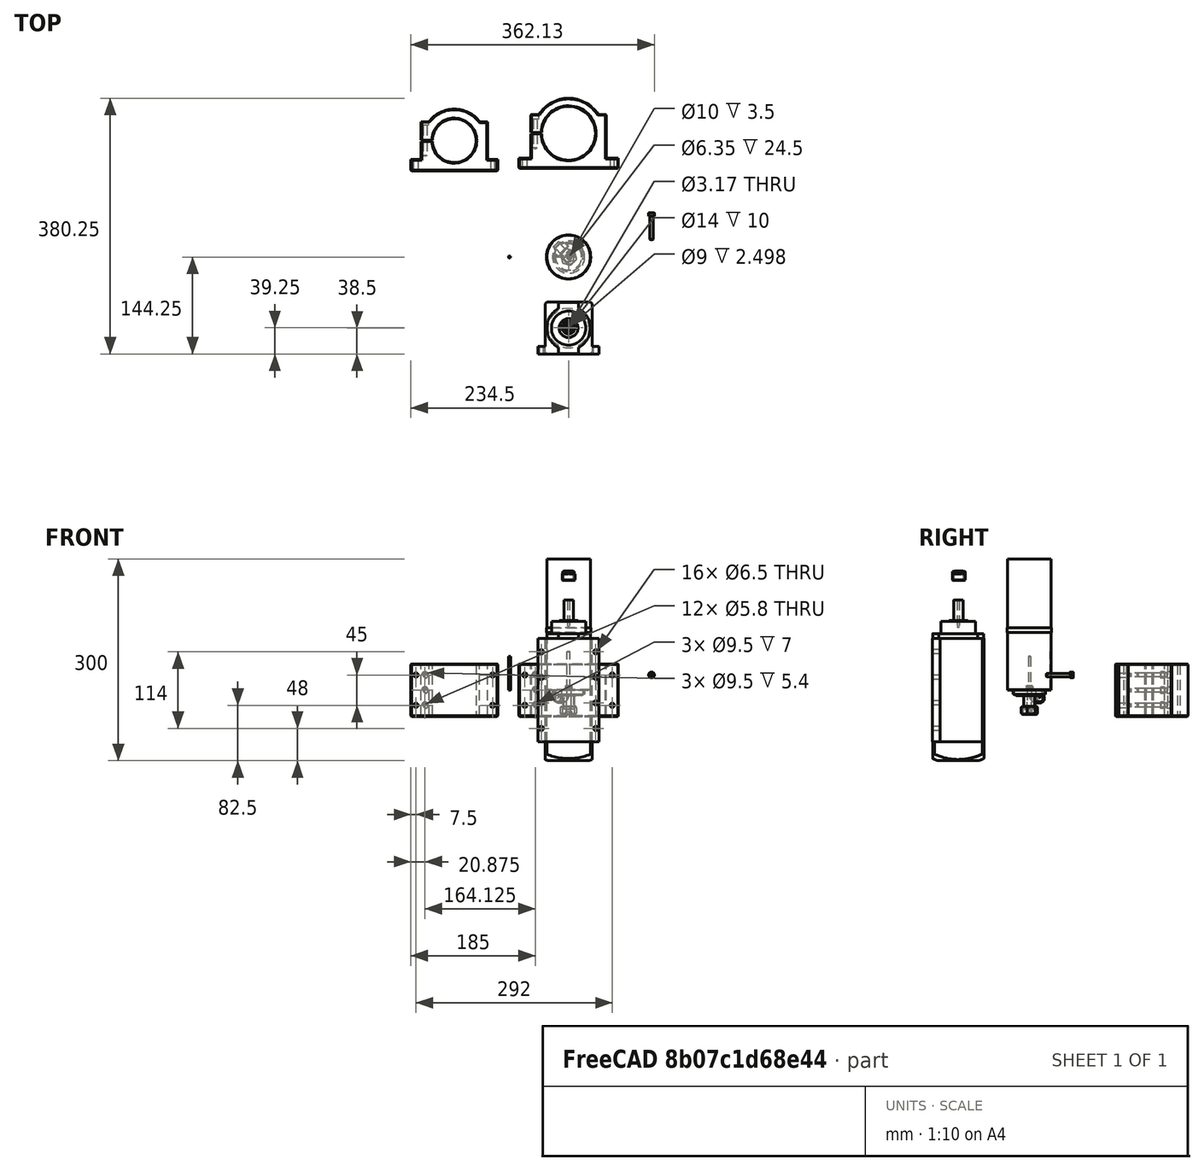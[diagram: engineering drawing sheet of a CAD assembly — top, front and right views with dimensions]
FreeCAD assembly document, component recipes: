
FREECAD ASSEMBLY — COMPONENT RECIPES ("Spindle")

This assembly document has 15 components, labeled P0..P14 below (a component is one placed body or linked part). 11 of them carry a construction recipe — the FreeCAD feature program that regenerates the part from scratch, quoted from this document or its linked companion documents; the rest are supplied as boundary geometry only. No exploded tour is included for this assembly.
COMPONENT P0 — recipe-attached ("80mm", modeled in this document).
Construction recipe (the document's own serialized feature program — sketch geometry with constraints, then the solid features built on it; lengths are millimeters unless a unit is written):

FEATURE [Sketcher::SketchObject] Sketch019
  FullyConstrained = true
  MapMode = 5
  Placement = pos=(0,0,0) rot=(1,0,0;1.5708rad)
  Support = -> [XZ_Plane005]
  sketch-geometry (18):
    g0: ArcOfCircle CenterX=0 CenterY=0 CenterZ=0 NormalX=0 NormalY=0 NormalZ=1 AngleXU=0 Radius=40 StartAngle=3.1666 EndAngle=9.39978
    g1: LineSegment StartX=-56 StartY=28 StartZ=0 EndX=-43.8178 EndY=28 EndZ=0
    g2: LineSegment StartX=56 StartY=28 StartZ=0 EndX=56 EndY=-37 EndZ=0
    g3: LineSegment StartX=-56 StartY=-37 StartZ=0 EndX=-56 EndY=-1 EndZ=0
    g4: LineSegment StartX=-74 StartY=-52 StartZ=0 EndX=74 EndY=-52 EndZ=0
    g5: LineSegment StartX=74 StartY=-52 StartZ=0 EndX=74 EndY=-37 EndZ=0
    g6: LineSegment StartX=74 StartY=-37 StartZ=0 EndX=56 EndY=-37 EndZ=0
    g7: LineSegment StartX=-74 StartY=-37 StartZ=0 EndX=-74 EndY=-52 EndZ=0
    g8: LineSegment StartX=-56 StartY=-37 StartZ=0 EndX=-74 EndY=-37 EndZ=0
    g9: LineSegment StartX=-56 StartY=1 StartZ=0 EndX=-39.9875 EndY=1 EndZ=0
    g10: LineSegment StartX=-39.9875 StartY=-1 StartZ=0 EndX=-56 EndY=-1 EndZ=0
    g11: GeomPoint [constr] X=0 Y=52 Z=0
    g12: LineSegment StartX=-56 StartY=1 StartZ=0 EndX=-56 EndY=28 EndZ=0
    g13: LineSegment [constr] StartX=-56 StartY=-1 StartZ=0 EndX=-56 EndY=1 EndZ=0
    g14: GeomPoint [constr] X=-56 Y=0 Z=0
    g15: ArcOfCircle CenterX=0 CenterY=0 CenterZ=0 NormalX=0 NormalY=0 NormalZ=1 AngleXU=0 Radius=52 StartAngle=0.56861 EndAngle=2.57298
    g16: LineSegment StartX=43.8178 StartY=28 StartZ=0 EndX=56 EndY=28 EndZ=0
    g17: GeomPoint [constr] X=0 Y=-52 Z=0
  constraints (45):
    c: Coincident(g0,g-1)
    c: Coincident(g16,g2)
    c: Coincident(g12,g1)
    c: Horizontal(g1)
    c: Vertical(g2)
    c: Vertical(g3)
    c: Coincident(g4,g5)
    c: Coincident(g5,g6)
    c: Coincident(g8,g7)
    c: Coincident(g7,g4)
    c: Horizontal(g4)
    c: Horizontal(g6)
    c: Vertical(g5)
    c: Vertical(g7)
    c: Diameter(g0) = 80
    c: DistanceY(g2,g2) = 65
    c: PointOnObject(g3,g6)
    c: Coincident(g6,g2)
    c: Tangent(g6,g8)
    c: PointOnObject(g8,g3)
    c: Horizontal(g9)
    c: Horizontal(g10)
    c: PointOnObject(g11,g-2)
    c: DistanceY(g4,g11) = 104
    c: DistanceY(g5,g5) = 15
    c: DistanceX(g4,g4) = 148
    c: Coincident(g3,g10)
    c: Coincident(g12,g9)
    c: Tangent(g3,g12)
    c: Coincident(g0,g10)
    c: Coincident(g0,g9)
    c: Coincident(g13,g3)
    c: Coincident(g13,g9)
    c: PointOnObject(g14,g-1)
    c: Symmetric(g9,g3,g14)
    c: DistanceY(g13,g13) = 2
    c: Tangent(g1,g16)
    c: Coincident(g15,g16)
    c: Coincident(g15,g1)
    c: PointOnObject(g11,g15)
    c: Coincident(g15,g0)
    c: Symmetric(g4,g4,g17)
    c: DistanceX(g8,g8) = 18
    c: Symmetric(g11,g17,g0)
    c: Equal(g16,g1)
FEATURE [PartDesign::Pad] Pad013
  ClaimChildren = false
  Direction = (1,1,1)
  Fit = 0
  FitJoin = 0
  InnerFit = 0
  InnerFitJoin = 0
  InnerTaperAngle = 0
  InnerTaperAngleRev = 0
  Length = 78
  Length2 = 100
  Linearize = true
  Midplane = true
  NewSolid = false
  Placement = pos=(0,0,0) rot=(1,0,0;1.5708rad)
  Profile = -> Sketch019
  Refine = true
  Suppress = false
  Type = 0
  _ProfileBasedVersion = 0
FEATURE [Sketcher::SketchObject] Sketch020
  ExternalGeometry = -> [Pad013]
  FullyConstrained = true
  MapMode = 5
  Placement = pos=(0,0,28) rot=(0,0,1;3.14159rad)
  Support = -> [Pad013]
  sketch-geometry (3):
    g0: Circle CenterX=49.5 CenterY=22.5 CenterZ=0 NormalX=0 NormalY=0 NormalZ=1 AngleXU=0 Radius=4.75
    g1: Circle CenterX=49.5 CenterY=0 CenterZ=0 NormalX=0 NormalY=0 NormalZ=1 AngleXU=0 Radius=4.75
    g2: Circle CenterX=49.5 CenterY=-22.5 CenterZ=0 NormalX=0 NormalY=0 NormalZ=1 AngleXU=0 Radius=4.75
  constraints (8):
    c: PointOnObject(g1,g-1)
    c: Vertical(g0,g1)
    c: Symmetric(g0,g2,g1)
    c: Equal(g0,g1)
    c: Equal(g1,g2)
    c: Diameter(g0) = 9.5
    c: DistanceY(g2,g0) = 45
    c: DistanceX(g1,g-3) = 6.5
FEATURE [PartDesign::Hole] Hole004
  BaseFeature = -> Pad013
  ClaimChildren = false
  CustomThreadClearance = 0
  Depth = 50
  DepthType = 0
  Diameter = 5.8
  DrillForDepth = false
  DrillPoint = 1
  DrillPointAngle = 118
  Fit = 0
  FitJoin = 0
  HoleCutCountersinkAngle = 90
  HoleCutCustomValues = false
  HoleCutDepth = 7
  HoleCutDiameter = 9.5
  HoleCutType = 1
  InnerFit = 0
  InnerFitJoin = 0
  ModelThread = false
  NewSolid = false
  Placement = pos=(0,0,0) rot=(1,0,0;1.5708rad)
  Profile = -> Sketch020
  Refine = true
  Suppress = false
  Tapered = false
  TaperedAngle = 90
  ThreadClass = 0
  ThreadDepth = 50
  ThreadDepthType = 0
  ThreadDirection = 0
  ThreadFit = 2
  ThreadSize = 13
  ThreadType = 1
  Threaded = false
  UseCustomThreadClearance = false
  _ProfileBasedVersion = 0
FEATURE [PartDesign::Chamfer] Chamfer003
  Angle = 45
  Base = -> Hole004 [Edge14,Edge18,Edge17,Edge48,Edge19,Edge54,Edge16,Edge3,Edge6,Edge24,Edge23,Edge22,Edge21,Edge20,Edge25,Edge29,Edge28,Edge30,Edge31,Edge32,Edge33,Edge34,Edge35,Edge7,Edge4,Edge27,Edge36,Edge57]
  BaseFeature = -> Hole004
  ChamferType = 0
  FlipDirection = false
  NewSolid = false
  Placement = pos=(0,0,0) rot=(1,0,0;1.5708rad)
  Refine = true
  Size = 1
  Size2 = 1
  SupportTransform = false
  Suppress = false
FEATURE [Sketcher::SketchObject] Sketch021
  ExternalGeometry = -> [Chamfer003]
  FullyConstrained = true
  MapMode = 5
  Placement = pos=(0,0,-37) rot=(0,0,1;3.14159rad)
  Support = -> [Chamfer003]
  sketch-geometry (3):
    g0: Circle CenterX=-65 CenterY=22.5 CenterZ=0 NormalX=0 NormalY=0 NormalZ=1 AngleXU=0 Radius=3.25
    g1: Circle CenterX=-65 CenterY=-22.5 CenterZ=0 NormalX=0 NormalY=0 NormalZ=1 AngleXU=0 Radius=3.25
    g2: GeomPoint [constr] X=-65 Y=0 Z=0
  constraints (7):
    c: Equal(g1,g0)
    c: Diameter(g0) = 6.5
    c: DistanceY(g1,g0) = 45
    c: DistanceX(g0,g-1) = 65
    c: PointOnObject(g2,g-1)
    c: Vertical(g0,g1)
    c: Symmetric(g0,g1,g2)
FEATURE [PartDesign::Pocket] Pocket003
  BaseFeature = -> Chamfer003
  ClaimChildren = false
  Fit = 0
  FitJoin = 0
  InnerFit = 0
  InnerFitJoin = 0
  InnerTaperAngle = 0
  InnerTaperAngleRev = 0
  Length = 5
  Length2 = 100
  Linearize = true
  NewSolid = false
  Placement = pos=(0,0,0) rot=(1,0,0;1.5708rad)
  Profile = -> Sketch021
  Refine = true
  Suppress = false
  Type = 1
  _ProfileBasedVersion = 0
FEATURE [PartDesign::Mirrored] Mirrored002
  BaseFeature = -> Pocket003
  CopyShape = false
  MirrorPlane = -> YZ_Plane005
  NewSolid = false
  OriginalSubs = -> [Pocket003]
  Originals = -> [Pocket003]
  ParallelTransform = true
  Placement = pos=(0,0,0) rot=(1,0,0;1.5708rad)
  Refine = true
  SubTransform = true
  Suppress = false
  _Version = 1
FEATURE [PartDesign::Body] Body005  label="80mm"
  AutoGroupSolids = false
  ExportMode = 0
  Group = -> [Sketch019,Pad013,Sketch020,Hole004,Chamfer003,Sketch021,Pocket003,Mirrored002]
  Origin = -> Origin005
  Placement = pos=(0,184,0) rot=(1,0,0;4.71239rad)
  Tip = -> Mirrored002
  _ExportChildren = -> [Pad013,Hole004,Chamfer003,Pocket003,Mirrored002]
  _GroupVersion = 1
COMPONENT P1 — recipe-attached ("1.5kw air001", modeled in this document).
Construction recipe (the document's own serialized feature program — sketch geometry with constraints, then the solid features built on it; lengths are millimeters unless a unit is written):

FEATURE [Sketcher::SketchObject] Sketch
  FullyConstrained = true
  MapMode = 5
  Support = -> [XY_Plane]
  sketch-geometry (8):
    g0: LineSegment StartX=-35 StartY=32.75 StartZ=0 EndX=35 EndY=32.75 EndZ=0
    g1: LineSegment StartX=35 StartY=32.75 StartZ=0 EndX=35 EndY=-32.75 EndZ=0
    g2: LineSegment StartX=-35 StartY=-32.75 StartZ=0 EndX=-35 EndY=32.75 EndZ=0
    g3: LineSegment StartX=-45.5 StartY=-32.75 StartZ=0 EndX=-35 EndY=-32.75 EndZ=0
    g4: LineSegment StartX=45.5 StartY=-32.75 StartZ=0 EndX=45.5 EndY=-44.25 EndZ=0
    g5: LineSegment StartX=45.5 StartY=-44.25 StartZ=0 EndX=-45.5 EndY=-44.25 EndZ=0
    g6: LineSegment StartX=-45.5 StartY=-44.25 StartZ=0 EndX=-45.5 EndY=-32.75 EndZ=0
    g7: LineSegment StartX=35 StartY=-32.75 StartZ=0 EndX=45.5 EndY=-32.75 EndZ=0
  constraints (22):
    c: Coincident(g0,g1)
    c: Coincident(g2,g0)
    c: Horizontal(g0)
    c: Vertical(g1)
    c: Vertical(g2)
    c: Coincident(g7,g4)
    c: Coincident(g4,g5)
    c: Coincident(g5,g6)
    c: Coincident(g6,g3)
    c: Horizontal(g3)
    c: Horizontal(g5)
    c: Vertical(g4)
    c: Vertical(g6)
    c: Symmetric(g2,g0,g-1)
    c: Coincident(g3,g2)
    c: Coincident(g7,g1)
    c: Tangent(g3,g7)
    c: Equal(g3,g7)
    c: DistanceX(g0,g0) = 70
    c: DistanceY(g4,g0) = 77
    c: DistanceX(g5,g4) = 91
    c: DistanceY(g4,g4) = 11.5
FEATURE [PartDesign::Pad] Pad
  ClaimChildren = false
  Direction = (1,1,1)
  Fit = 0
  FitJoin = 0
  InnerFit = 0
  InnerFitJoin = 0
  InnerTaperAngle = 0
  InnerTaperAngleRev = 0
  Length = 154
  Length2 = 100
  Linearize = true
  Midplane = true
  NewSolid = false
  Profile = -> Sketch
  Refine = true
  Suppress = false
  Type = 0
  _ProfileBasedVersion = 0
FEATURE [Sketcher::SketchObject] Sketch001
  ExternalGeometry = -> [Pad]
  FullyConstrained = true
  MapMode = 5
  Placement = pos=(0,0,77) rot=(0,0,1;0rad)
  Support = -> [Pad]
  sketch-geometry (18):
    g0: ArcOfCircle CenterX=0 CenterY=-5.75 CenterZ=0 NormalX=0 NormalY=0 NormalZ=1 AngleXU=0 Radius=32.5 StartAngle=2.05052 EndAngle=4.23266
    g1: LineSegment StartX=15 StartY=30.25 StartZ=0 EndX=15 EndY=23.0814 EndZ=0
    g2: LineSegment StartX=-15 StartY=23.0814 StartZ=0 EndX=-15 EndY=30.25 EndZ=0
    g3: LineSegment StartX=-13 StartY=-43.75 StartZ=0 EndX=13 EndY=-43.75 EndZ=0
    g4: LineSegment StartX=15 StartY=-41.75 StartZ=0 EndX=15 EndY=-34.5814 EndZ=0
    g5: LineSegment StartX=-15 StartY=-34.5814 StartZ=0 EndX=-15 EndY=-41.75 EndZ=0
    g6: ArcOfCircle CenterX=13 CenterY=-41.75 CenterZ=0 NormalX=0 NormalY=0 NormalZ=1 AngleXU=0 Radius=2 StartAngle=4.71239 EndAngle=6.28319
    g7: GeomPoint [constr] X=15 Y=-43.75 Z=0
    g8: ArcOfCircle CenterX=-13 CenterY=-41.75 CenterZ=0 NormalX=0 NormalY=0 NormalZ=1 AngleXU=0 Radius=2 StartAngle=3.14159 EndAngle=4.71239
    g9: GeomPoint [constr] X=-15 Y=-43.75 Z=0
    g10: ArcOfCircle CenterX=0 CenterY=-5.75 CenterZ=0 NormalX=0 NormalY=0 NormalZ=1 AngleXU=0 Radius=32.5 StartAngle=5.19212 EndAngle=7.37425
    g11: GeomPoint [constr] X=0 Y=-43.75 Z=0
    g12: LineSegment StartX=-13 StartY=32.25 StartZ=0 EndX=13 EndY=32.25 EndZ=0
    g13: GeomPoint [constr] X=0 Y=32.25 Z=0
    g14: ArcOfCircle CenterX=-13 CenterY=30.25 CenterZ=0 NormalX=0 NormalY=0 NormalZ=1 AngleXU=0 Radius=2 StartAngle=1.5708 EndAngle=3.14159
    g15: GeomPoint [constr] X=-15 Y=32.25 Z=0
    g16: ArcOfCircle CenterX=13 CenterY=30.25 CenterZ=0 NormalX=0 NormalY=0 NormalZ=1 AngleXU=0 Radius=2 StartAngle=3e-16 EndAngle=1.5708
    g17: GeomPoint [constr] X=15 Y=32.25 Z=0
  constraints (43):
    c: Diameter(g0) = 65
    c: PointOnObject(g0,g-2)
    c: Vertical(g1)
    c: Vertical(g2)
    c: Vertical(g4)
    c: Vertical(g5)
    c: Vertical(g4,g1)
    c: Vertical(g5,g2)
    c: Tangent(g3,g6) = -1.5708
    c: Tangent(g4,g6) = -1.5708
    c: Tangent(g3,g8) = -1.5708
    c: Tangent(g5,g8) = -1.5708
    c: Coincident(g0,g2)
    c: Coincident(g10,g1)
    c: Equal(g0,g10)
    c: Coincident(g0,g5)
    c: Coincident(g10,g4)
    c: Coincident(g0,g10)
    c: Vertical(g7,g4)
    c: Horizontal(g7,g3)
    c: Horizontal(g9,g3)
    c: Vertical(g5,g9)
    c: PointOnObject(g11,g3)
    c: PointOnObject(g11,g-2)
    c: Symmetric(g9,g7,g11)
    c: Horizontal(g12)
    c: PointOnObject(g13,g12)
    c: Symmetric(g13,g11,g0)
    c: PointOnObject(g15,g2)
    c: PointOnObject(g15,g12)
    c: Tangent(g2,g14) = 1.5708
    c: Tangent(g12,g14) = 1.5708
    c: PointOnObject(g17,g1)
    c: PointOnObject(g17,g12)
    c: Tangent(g1,g16) = 1.5708
    c: Tangent(g12,g16) = 1.5708
    c: Equal(g6,g8)
    c: Equal(g8,g14)
    c: Equal(g14,g16)
    c: Diameter(g14) = 4
    c: DistanceY(g13,g-3) = 0.5
    c: DistanceX(g15,g17) = 30
    c: DistanceY(g-4,g11) = 0.5
FEATURE [PartDesign::Pad] Pad001
  BaseFeature = -> Pad
  ClaimChildren = false
  Direction = (1,1,1)
  Fit = 0
  FitJoin = 0
  InnerFit = 0
  InnerFitJoin = 0
  InnerTaperAngle = 0
  InnerTaperAngleRev = 0
  Length = 7
  Length2 = 100
  Linearize = true
  NewSolid = false
  Profile = -> Sketch001
  Refine = true
  Suppress = false
  Type = 0
  _ProfileBasedVersion = 0
FEATURE [Sketcher::SketchObject] Sketch002
  ExternalGeometry = -> [Pad001]
  FullyConstrained = true
  MapMode = 5
  Placement = pos=(0,0,84) rot=(0,0,1;0rad)
  Support = -> [Pad001]
  sketch-geometry (1):
    g0: Circle CenterX=0 CenterY=-5.75 CenterZ=0 NormalX=0 NormalY=0 NormalZ=1 AngleXU=0 Radius=25.5
  constraints (2):
    c: Coincident(g0,g-3)
    c: Diameter(g0) = 51
FEATURE [PartDesign::Pad] Pad002
  BaseFeature = -> Pad001
  ClaimChildren = false
  Direction = (1,1,1)
  Fit = 0
  FitJoin = 0
  InnerFit = 0
  InnerFitJoin = 0
  InnerTaperAngle = 0
  InnerTaperAngleRev = 0
  Length = 18
  Length2 = 100
  Linearize = true
  NewSolid = false
  Profile = -> Sketch002
  Refine = true
  Suppress = false
  Type = 0
  _ProfileBasedVersion = 0
FEATURE [PartDesign::Chamfer] Chamfer
  Angle = 45
  Base = -> Pad002 [Edge1,Edge2]
  BaseFeature = -> Pad002
  ChamferType = 0
  FlipDirection = false
  NewSolid = false
  Refine = true
  Size = 2.5
  Size2 = 1
  SupportTransform = false
  Suppress = false
FEATURE [Sketcher::SketchObject] Sketch003
  ExternalGeometry = -> [Chamfer]
  FullyConstrained = true
  MapMode = 5
  Placement = pos=(0,0,-77) rot=(1,0,0;3.14159rad)
  Support = -> [Chamfer]
  sketch-geometry (8):
    g0: LineSegment StartX=34.9 StartY=-30.25 StartZ=0 EndX=34.9 EndY=41.35 EndZ=0
    g1: LineSegment StartX=-34.9 StartY=41.35 StartZ=0 EndX=-34.9 EndY=-30.25 EndZ=0
    g2: LineSegment StartX=-32.5 StartY=-32.65 StartZ=0 EndX=32.5 EndY=-32.65 EndZ=0
    g3: LineSegment StartX=32.5 StartY=-32.65 StartZ=0 EndX=34.9 EndY=-30.25 EndZ=0
    g4: LineSegment StartX=-32.5 StartY=-32.65 StartZ=0 EndX=-34.9 EndY=-30.25 EndZ=0
    g5: LineSegment StartX=-32.5 StartY=43.75 StartZ=0 EndX=32.5 EndY=43.75 EndZ=0
    g6: LineSegment StartX=-34.9 StartY=41.35 StartZ=0 EndX=-32.5 EndY=43.75 EndZ=0
    g7: LineSegment StartX=34.9 StartY=41.35 StartZ=0 EndX=32.5 EndY=43.75 EndZ=0
  constraints (24):
    c: Vertical(g0)
    c: Vertical(g1)
    c: DistanceX(g0,g-5) = 0.1
    c: DistanceX(g-3,g1) = 0.1
    c: Horizontal(g2)
    c: Coincident(g3,g2)
    c: Coincident(g3,g0)
    c: Coincident(g4,g2)
    c: Coincident(g4,g1)
    c: Vertical(g2,g-4)
    c: Vertical(g-4,g2)
    c: Horizontal(g-5,g0)
    c: Horizontal(g1,g-3)
    c: DistanceY(g-4,g2) = 0.1
    c: Horizontal(g5)
    c: Coincident(g6,g1)
    c: Coincident(g6,g5)
    c: Coincident(g7,g0)
    c: Coincident(g7,g5)
    c: Vertical(g2,g5)
    c: Vertical(g5,g2)
    c: Equal(g6,g7)
    c: Equal(g7,g3)
    c: DistanceY(g5,g-6) = 0.5
FEATURE [PartDesign::Pad] Pad003
  BaseFeature = -> Chamfer
  ClaimChildren = false
  Direction = (1,1,1)
  Fit = 0
  FitJoin = 0
  InnerFit = 0
  InnerFitJoin = 0
  InnerTaperAngle = 0
  InnerTaperAngleRev = 0
  Length = 28
  Length2 = 100
  Linearize = true
  NewSolid = false
  Profile = -> Sketch003
  Refine = true
  Suppress = false
  Type = 0
  _ProfileBasedVersion = 0
FEATURE [Sketcher::SketchObject] Sketch004
  ExternalGeometry = -> [Pad003]
  FullyConstrained = true
  MapMode = 5
  Placement = pos=(0,0,0) rot=(1,0,0;1.5708rad)
  Support = -> [XZ_Plane]
  sketch-geometry (3):
    g0: ArcOfCircle CenterX=-1.65e-14 CenterY=-20 CenterZ=0 NormalX=0 NormalY=0 NormalZ=1 AngleXU=0 Radius=90 StartAngle=4.71239 EndAngle=5.5194
    g1: LineSegment StartX=-1.65e-14 StartY=-110 StartZ=0 EndX=65 EndY=-110 EndZ=0
    g2: LineSegment StartX=65 StartY=-82.2495 StartZ=0 EndX=65 EndY=-110 EndZ=0
  constraints (10):
    c: PointOnObject(g0,g-2)
    c: Vertical(g0,g0)
    c: Horizontal(g1)
    c: Coincident(g2,g0)
    c: Coincident(g2,g1)
    c: Vertical(g2)
    c: Diameter(g0) = 180
    c: Coincident(g1,g0)
    c: DistanceX(g1,g1) = 65
    c: DistanceY(g0,g-1) = 20
FEATURE [PartDesign::Line] DatumLine
  AttacherType = Attacher::AttachEngineLine
  Length = 239
  MapMode = 42
  MinimumLength = 10
  Placement = pos=(0,-5.75,0) rot=(0,0,1;0rad)
  ResizeMode = 0
  Support = -> [Pad003]
FEATURE [PartDesign::Groove] Groove
  Angle = 360
  Axis = (0,0,1)
  Base = (0,-5.75,0)
  BaseFeature = -> Pad003
  ClaimChildren = false
  Fit = 0
  FitJoin = 0
  InnerFit = 0
  InnerFitJoin = 0
  NewSolid = false
  Profile = -> Sketch004
  ReferenceAxis = -> DatumLine
  Refine = true
  Suppress = false
  _ProfileBasedVersion = 0
FEATURE [Sketcher::SketchObject] Sketch005
  ExternalGeometry = -> [Groove]
  FullyConstrained = true
  MapMode = 5
  Placement = pos=(0,-44.25,0) rot=(1,0,0;1.5708rad)
  Support = -> [Groove]
  sketch-geometry (7):
    g0: Circle CenterX=-40.5 CenterY=57 CenterZ=0 NormalX=0 NormalY=0 NormalZ=1 AngleXU=0 Radius=3.25
    g1: Circle CenterX=-40.5 CenterY=19 CenterZ=0 NormalX=0 NormalY=0 NormalZ=1 AngleXU=0 Radius=3.25
    g2: Circle CenterX=-40.5 CenterY=-19 CenterZ=0 NormalX=0 NormalY=0 NormalZ=1 AngleXU=0 Radius=3.25
    g3: Circle CenterX=-40.5 CenterY=-57 CenterZ=0 NormalX=0 NormalY=0 NormalZ=1 AngleXU=0 Radius=3.25
    g4: LineSegment [constr] StartX=-40.5 StartY=57 StartZ=0 EndX=-40.5 EndY=19 EndZ=0
    g5: LineSegment [constr] StartX=-40.5 StartY=19 StartZ=0 EndX=-40.5 EndY=-19 EndZ=0
    g6: LineSegment [constr] StartX=-40.5 StartY=-19 StartZ=0 EndX=-40.5 EndY=-57 EndZ=0
  constraints (18):
    c: Equal(g0,g1)
    c: Equal(g1,g2)
    c: Equal(g2,g3)
    c: Vertical(g0,g1)
    c: Vertical(g1,g2)
    c: Vertical(g2,g3)
    c: Coincident(g4,g0)
    c: Coincident(g4,g1)
    c: Coincident(g5,g1)
    c: Coincident(g5,g2)
    c: Coincident(g6,g2)
    c: Coincident(g6,g3)
    c: Equal(g4,g5)
    c: Equal(g5,g6)
    c: DistanceY(g4,g4) = 38
    c: DistanceY(g0,g-3) = 20
    c: DistanceX(g0,g-1) = 40.5
    c: Diameter(g0) = 6.5
FEATURE [PartDesign::Pocket] Pocket
  BaseFeature = -> Groove
  ClaimChildren = false
  Fit = 0
  FitJoin = 0
  InnerFit = 0
  InnerFitJoin = 0
  InnerTaperAngle = 0
  InnerTaperAngleRev = 0
  Length = 5
  Length2 = 100
  Linearize = true
  NewSolid = false
  Profile = -> Sketch005
  Refine = true
  Suppress = false
  Type = 1
  _ProfileBasedVersion = 0
FEATURE [PartDesign::Mirrored] Mirrored
  BaseFeature = -> Pocket
  CopyShape = false
  MirrorPlane = -> YZ_Plane
  NewSolid = false
  OriginalSubs = -> [Pocket]
  Originals = -> [Pocket]
  ParallelTransform = true
  Refine = true
  SubTransform = true
  Suppress = false
  _Version = 1
FEATURE [Sketcher::SketchObject] Sketch006
  ExternalGeometry = -> [Mirrored]
  FullyConstrained = true
  MapMode = 5
  Placement = pos=(0,0,102) rot=(0,0,1;0rad)
  Support = -> [Mirrored]
  sketch-geometry (1):
    g0: Circle CenterX=0 CenterY=-5.75 CenterZ=0 NormalX=0 NormalY=0 NormalZ=1 AngleXU=0 Radius=7
  constraints (2):
    c: Coincident(g0,g-3)
    c: Diameter(g0) = 14
FEATURE [PartDesign::Pad] Pad004
  BaseFeature = -> Mirrored
  ClaimChildren = false
  Direction = (1,1,1)
  Fit = 0
  FitJoin = 0
  InnerFit = 0
  InnerFitJoin = 0
  InnerTaperAngle = 0
  InnerTaperAngleRev = 0
  Length = 32
  Length2 = 100
  Linearize = true
  NewSolid = false
  Profile = -> Sketch006
  Refine = true
  Suppress = false
  Type = 0
  _ProfileBasedVersion = 0
FEATURE [Sketcher::SketchObject] Sketch007
  ExternalGeometry = -> [Pad004]
  FullyConstrained = true
  MapMode = 5
  Placement = pos=(0,0,102) rot=(0,0,1;0rad)
  Support = -> [Pad004]
  sketch-geometry (1):
    g0: Circle CenterX=0 CenterY=-5.75 CenterZ=0 NormalX=0 NormalY=0 NormalZ=1 AngleXU=0 Radius=14
  constraints (2):
    c: Coincident(g0,g-3)
    c: Diameter(g0) = 28
FEATURE [PartDesign::Pad] Pad005
  BaseFeature = -> Pad004
  ClaimChildren = false
  ColoredElements = -> Pad005 [Face13,Face14,Face15,Face16,Face17,Face18,Face19,Face20,Face41,Face43]
  Direction = (1,1,1)
  Fit = 0
  FitJoin = 0
  InnerFit = 0
  InnerFitJoin = 0
  InnerTaperAngle = 0
  InnerTaperAngleRev = 0
  Length = 1.5
  Length2 = 100
  Linearize = true
  NewSolid = false
  Profile = -> Sketch007
  Refine = true
  Suppress = false
  Type = 0
  _ProfileBasedVersion = 0
FEATURE [PartDesign::Hole] Hole001
  BaseFeature = -> Pad005
  ClaimChildren = false
  CustomThreadClearance = 0
  Depth = 40
  DepthType = 0
  Diameter = 3.175
  DrillForDepth = false
  DrillPoint = 1
  DrillPointAngle = 118
  Fit = 0
  FitJoin = 0
  HoleCutCountersinkAngle = 90
  HoleCutCustomValues = false
  HoleCutDepth = 0
  HoleCutDiameter = 6.1
  HoleCutType = 0
  InnerFit = 0
  InnerFitJoin = 0
  ModelThread = false
  NewSolid = false
  Profile = -> Pad005 [Edge126]
  Refine = true
  Suppress = false
  Tapered = false
  TaperedAngle = 90
  ThreadClass = 0
  ThreadDepth = 40
  ThreadDepthType = 0
  ThreadDirection = 0
  ThreadFit = 0
  ThreadSize = 0
  ThreadType = 0
  Threaded = false
  UseCustomThreadClearance = false
  _ProfileBasedVersion = 0
FEATURE [PartDesign::Body] Body  label="1.5kw air"
  AutoGroupSolids = false
  ExportMode = 0
  Group = -> [Sketch,Pad,Sketch001,Pad001,Sketch002,Pad002,Chamfer,Sketch003,Pad003,Sketch004,Groove,DatumLine,Sketch005,Pocket,Mirrored,Sketch006,Pad004,Sketch007,Pad005,Hole001]
  Origin = -> Origin
  Placement = pos=(0,-100,0) rot=(0,0,1;0rad)
  Tip = -> Hole001
  _ExportChildren = -> [Pad,Pad001,Pad002,Chamfer,Pad003,Groove,DatumLine,Pocket,Mirrored,Pad004,Hole001]
  _GroupVersion = 1
COMPONENT P2 — recipe-attached ("ER11 nut", modeled in this document).
Construction recipe (the document's own serialized feature program — sketch geometry with constraints, then the solid features built on it; lengths are millimeters unless a unit is written):

FEATURE [Sketcher::SketchObject] Sketch008
  FullyConstrained = true
  MapMode = 5
  Support = -> [XY_Plane001]
  sketch-geometry (1):
    g0: Circle CenterX=0 CenterY=0 CenterZ=0 NormalX=0 NormalY=0 NormalZ=1 AngleXU=0 Radius=9.5
  constraints (2):
    c: Coincident(g0,g-1)
    c: Diameter(g0) = 19
FEATURE [PartDesign::Pad] Pad006
  ClaimChildren = false
  Direction = (1,1,1)
  Fit = 0
  FitJoin = 0
  InnerFit = 0
  InnerFitJoin = 0
  InnerTaperAngle = 0
  InnerTaperAngleRev = 0
  Length = 10
  Length2 = 100
  Linearize = true
  NewSolid = false
  Profile = -> Sketch008
  Refine = true
  Suppress = false
  Type = 0
  _ProfileBasedVersion = 0
FEATURE [Sketcher::SketchObject] Sketch009
  FullyConstrained = true
  MapMode = 5
  Placement = pos=(0,0,10) rot=(0,0,1;0rad)
  Support = -> [Pad006]
  sketch-geometry (18):
    g0: LineSegment StartX=8.5 StartY=-4.24264 StartZ=0 EndX=8.5 EndY=4.24264 EndZ=0
    g1: LineSegment StartX=7.92423 StartY=5.2399 StartZ=0 EndX=0.575765 EndY=9.48254 EndZ=0
    g2: LineSegment StartX=-0.575765 StartY=9.48254 StartZ=0 EndX=-7.92423 EndY=5.2399 EndZ=0
    g3: LineSegment StartX=-8.5 StartY=4.24264 StartZ=0 EndX=-8.5 EndY=-4.24264 EndZ=0
    g4: LineSegment StartX=-7.92423 StartY=-5.2399 StartZ=0 EndX=-0.575765 EndY=-9.48254 EndZ=0
    g5: LineSegment StartX=0.575765 StartY=-9.48254 StartZ=0 EndX=7.92423 EndY=-5.2399 EndZ=0
    g6: ArcOfCircle CenterX=0 CenterY=0 CenterZ=0 NormalX=0 NormalY=0 NormalZ=1 AngleXU=0 Radius=9.5 StartAngle=2.55735 EndAngle=2.67864
    g7: ArcOfCircle CenterX=0 CenterY=0 CenterZ=0 NormalX=0 NormalY=0 NormalZ=1 AngleXU=0 Radius=9.5 StartAngle=1.51015 EndAngle=1.63144
    g8: ArcOfCircle CenterX=0 CenterY=0 CenterZ=0 NormalX=0 NormalY=0 NormalZ=1 AngleXU=0 Radius=9.5 StartAngle=0.462955 EndAngle=0.584243
    g9: ArcOfCircle CenterX=0 CenterY=0 CenterZ=0 NormalX=0 NormalY=0 NormalZ=1 AngleXU=0 Radius=9.5 StartAngle=5.69894 EndAngle=5.82023
    g10: ArcOfCircle CenterX=0 CenterY=0 CenterZ=0 NormalX=0 NormalY=0 NormalZ=1 AngleXU=0 Radius=9.5 StartAngle=4.65174 EndAngle=4.77303
    g11: ArcOfCircle CenterX=0 CenterY=0 CenterZ=0 NormalX=0 NormalY=0 NormalZ=1 AngleXU=0 Radius=9.5 StartAngle=3.60455 EndAngle=3.72584
    g12: LineSegment [constr] StartX=-7.92423 StartY=5.2399 StartZ=0 EndX=-8.5 EndY=4.24264 EndZ=0
    g13: LineSegment [constr] StartX=-0.575765 StartY=9.48254 StartZ=0 EndX=0.575765 EndY=9.48254 EndZ=0
    g14: LineSegment [constr] StartX=8.5 StartY=4.24264 StartZ=0 EndX=7.92423 EndY=5.2399 EndZ=0
    g15: LineSegment [constr] StartX=7.92423 StartY=-5.2399 StartZ=0 EndX=8.5 EndY=-4.24264 EndZ=0
    g16: LineSegment [constr] StartX=-0.575765 StartY=-9.48254 StartZ=0 EndX=0.575765 EndY=-9.48254 EndZ=0
    g17: LineSegment [constr] StartX=-7.92423 StartY=-5.2399 StartZ=0 EndX=-8.5 EndY=-4.24264 EndZ=0
  constraints (48):
    c: Vertical(g0)
    c: Diameter(g6) = 19
    c: Equal(g5,g4)
    c: Equal(g4,g3)
    c: Equal(g3,g0)
    c: Equal(g0,g1)
    c: Equal(g1,g2)
    c: DistanceX(g3,g0) = 17
    c: Coincident(g6,g-1)
    c: Vertical(g3)
    c: Symmetric(g1,g2,g-2)
    c: Symmetric(g4,g5,g-2)
    c: Coincident(g6,g2)
    c: Coincident(g7,g2)
    c: Equal(g6,g7)
    c: Coincident(g8,g1)
    c: PointOnObject(g7,g1)
    c: Coincident(g6,g7)
    c: Equal(g6,g8)
    c: Coincident(g9,g0)
    c: Coincident(g8,g0)
    c: Coincident(g6,g8)
    c: Coincident(g10,g5)
    c: Coincident(g9,g5)
    c: Coincident(g6,g9)
    c: Equal(g6,g10)
    c: Coincident(g11,g4)
    c: PointOnObject(g10,g4)
    c: Coincident(g6,g10)
    c: Equal(g6,g11)
    c: Coincident(g6,g3)
    c: Coincident(g11,g3)
    c: Coincident(g6,g11)
    c: Parallel(g5,g2)
    c: Coincident(g12,g2)
    c: Coincident(g12,g3)
    c: Coincident(g13,g2)
    c: Coincident(g13,g1)
    c: Coincident(g14,g0)
    c: Coincident(g1,g14)
    c: Coincident(g15,g5)
    c: Coincident(g0,g15)
    c: Coincident(g16,g4)
    c: Coincident(g16,g5)
    c: Coincident(g17,g4)
    c: Coincident(g17,g3)
    c: Equal(g12,g13)
    c: Equal(g13,g14)
FEATURE [PartDesign::Pad] Pad007
  BaseFeature = -> Pad006
  ClaimChildren = false
  Direction = (1,1,1)
  Fit = 0
  FitJoin = 0
  InnerFit = 0
  InnerFitJoin = 0
  InnerTaperAngle = 0
  InnerTaperAngleRev = 0
  Length = 4
  Length2 = 100
  Linearize = true
  NewSolid = false
  Profile = -> Sketch009
  Refine = true
  Suppress = false
  Type = 0
  _ProfileBasedVersion = 0
FEATURE [Sketcher::SketchObject] Sketch010
  ExternalGeometry = -> [Pad007]
  FullyConstrained = true
  MapMode = 5
  Placement = pos=(0,0,0) rot=(1,0,0;1.5708rad)
  Support = -> [XZ_Plane001]
  sketch-geometry (4):
    g0: ArcOfCircle CenterX=0 CenterY=-20.4819 CenterZ=0 NormalX=0 NormalY=0 NormalZ=1 AngleXU=0 Radius=35 StartAngle=1.25109 EndAngle=1.5708
    g1: GeomPoint [constr] X=6 Y=14 Z=0
    g2: LineSegment StartX=2.1e-15 StartY=14.5181 StartZ=0 EndX=11 EndY=14.5181 EndZ=0
    g3: LineSegment StartX=11 StartY=14.5181 StartZ=0 EndX=11 EndY=12.7446 EndZ=0
  constraints (12):
    c: PointOnObject(g0,g-2)
    c: PointOnObject(g0,g-2)
    c: PointOnObject(g1,g0)
    c: Horizontal(g1,g-3)
    c: DistanceX(g-1,g1) = 6
    c: Radius(g0) = 35
    c: DistanceX(g-1,g0) = 11
    c: Coincident(g2,g0)
    c: Horizontal(g2)
    c: Coincident(g3,g2)
    c: Coincident(g3,g0)
    c: Vertical(g3)
FEATURE [PartDesign::Groove] Groove001
  Angle = 360
  Axis = (-3e-16,3e-16,1)
  Base = (0,0,0)
  BaseFeature = -> Pad007
  ClaimChildren = false
  Fit = 0
  FitJoin = 0
  InnerFit = 0
  InnerFitJoin = 0
  NewSolid = false
  Profile = -> Sketch010
  ReferenceAxis = -> Z_Axis001
  Refine = true
  Suppress = false
  _ProfileBasedVersion = 0
FEATURE [Sketcher::SketchObject] Sketch011
  FullyConstrained = true
  MapMode = 5
  Placement = pos=(0,0,14) rot=(0,0,1;0rad)
  Support = -> [Groove001]
  sketch-geometry (1):
    g0: Circle CenterX=0 CenterY=0 CenterZ=0 NormalX=0 NormalY=0 NormalZ=1 AngleXU=0 Radius=4.5
  constraints (2):
    c: Coincident(g0,g-1)
    c: Diameter(g0) = 9
FEATURE [PartDesign::Pocket] Pocket001
  BaseFeature = -> Groove001
  ClaimChildren = false
  Fit = 0
  FitJoin = 0
  InnerFit = 0
  InnerFitJoin = 0
  InnerTaperAngle = 0
  InnerTaperAngleRev = 0
  Length = 5
  Length2 = 100
  Linearize = true
  NewSolid = false
  Profile = -> Sketch011
  Refine = true
  Suppress = false
  Type = 1
  _ProfileBasedVersion = 0
FEATURE [PartDesign::Hole] Hole
  BaseFeature = -> Pocket001
  ClaimChildren = false
  CustomThreadClearance = 0
  Depth = 10
  DepthType = 0
  Diameter = 14
  DrillForDepth = false
  DrillPoint = 1
  DrillPointAngle = 118
  Fit = 0
  FitJoin = 0
  HoleCutCountersinkAngle = 90
  HoleCutCustomValues = false
  HoleCutDepth = 0
  HoleCutDiameter = 14.1
  HoleCutType = 0
  InnerFit = 0
  InnerFitJoin = 0
  ModelThread = false
  NewSolid = false
  Profile = -> Pocket001 [Edge39]
  Refine = true
  Reversed = true
  Suppress = false
  Tapered = false
  TaperedAngle = 90
  ThreadClass = 0
  ThreadDepth = 10
  ThreadDepthType = 0
  ThreadDirection = 0
  ThreadFit = 0
  ThreadSize = 0
  ThreadType = 0
  Threaded = false
  UseCustomThreadClearance = false
  _ProfileBasedVersion = 0
FEATURE [PartDesign::Chamfer] Chamfer001
  Angle = 45
  Base = -> Hole [Edge10]
  BaseFeature = -> Hole
  ChamferType = 0
  FlipDirection = false
  NewSolid = false
  Refine = true
  Size = 1
  Size2 = 1
  SupportTransform = false
  Suppress = false
FEATURE [PartDesign::Body] Body001  label="ER11"
  AutoGroupSolids = false
  ExportMode = 0
  Group = -> [Sketch008,Pad006,Sketch009,Pad007,Sketch010,Groove001,Sketch011,Pocket001,Hole,Chamfer001]
  Origin = -> Origin001
  Placement = pos=(0,-105,163) rot=(0,0,1;0rad)
  Tip = -> Chamfer001
  _ExportChildren = -> [Pad006,Pad007,Groove001,Hole,Chamfer001]
  _GroupVersion = 1
COMPONENT P3 — recipe-attached ("Link002(Tool)", modeled in this document).
Construction recipe (the document's own serialized feature program — sketch geometry with constraints, then the solid features built on it; lengths are millimeters unless a unit is written):

FEATURE [Sketcher::SketchObject] Sketch012
  FullyConstrained = true
  MapMode = 5
  Support = -> [XY_Plane002]
  sketch-geometry (1):
    g0: Circle CenterX=0 CenterY=0 CenterZ=0 NormalX=0 NormalY=0 NormalZ=1 AngleXU=0 Radius=1.5875
  constraints (2):
    c: Coincident(g0,g-1)
    c: Diameter(g0) = 3.175
FEATURE [PartDesign::Pad] Pad008
  ClaimChildren = false
  Direction = (1,1,1)
  Fit = 0
  FitJoin = 0
  InnerFit = 0
  InnerFitJoin = 0
  InnerTaperAngle = 0
  InnerTaperAngleRev = 0
  Length = 50
  Length2 = 100
  Linearize = true
  NewSolid = false
  Profile = -> Sketch012
  Refine = true
  Suppress = false
  Type = 0
  _ProfileBasedVersion = 0
FEATURE [PartDesign::Body] Body002  label="Tool"
  AutoGroupSolids = false
  ExportMode = 0
  Group = -> [Sketch012,Pad008]
  Origin = -> Origin002
  Placement = pos=(-88,0,0) rot=(0,0,1;0rad)
  Tip = -> Pad008
  _ExportChildren = -> [Pad008]
  _GroupVersion = 1
COMPONENT P4 — recipe-attached ("Link003(65mm bracket)", modeled in this document).
Construction recipe (the document's own serialized feature program — sketch geometry with constraints, then the solid features built on it; lengths are millimeters unless a unit is written):

FEATURE [Sketcher::SketchObject] Sketch016
  FullyConstrained = true
  MapMode = 5
  Placement = pos=(0,0,0) rot=(1,0,0;1.5708rad)
  Support = -> [XZ_Plane004]
  sketch-geometry (18):
    g0: ArcOfCircle CenterX=0 CenterY=0 CenterZ=0 NormalX=0 NormalY=0 NormalZ=1 AngleXU=0 Radius=32.5 StartAngle=3.17237 EndAngle=9.394
    g1: LineSegment StartX=-49.5 StartY=28 StartZ=0 EndX=-37.7492 EndY=28 EndZ=0
    g2: LineSegment StartX=49.5 StartY=28 StartZ=0 EndX=49.5 EndY=-28 EndZ=0
    g3: LineSegment StartX=-49.5 StartY=-28 StartZ=0 EndX=-49.5 EndY=-1 EndZ=0
    g4: LineSegment StartX=-64.5 StartY=-45 StartZ=0 EndX=64.5 EndY=-45 EndZ=0
    g5: LineSegment StartX=64.5 StartY=-45 StartZ=0 EndX=64.5 EndY=-28 EndZ=0
    g6: LineSegment StartX=64.5 StartY=-28 StartZ=0 EndX=49.5 EndY=-28 EndZ=0
    g7: LineSegment StartX=-64.5 StartY=-28 StartZ=0 EndX=-64.5 EndY=-45 EndZ=0
    g8: LineSegment StartX=-49.5 StartY=-28 StartZ=0 EndX=-64.5 EndY=-28 EndZ=0
    g9: LineSegment StartX=-49.5 StartY=1 StartZ=0 EndX=-32.4846 EndY=1 EndZ=0
    g10: LineSegment StartX=-32.4846 StartY=-1 StartZ=0 EndX=-49.5 EndY=-1 EndZ=0
    g11: GeomPoint [constr] X=0 Y=47 Z=0
    g12: LineSegment StartX=-49.5 StartY=1 StartZ=0 EndX=-49.5 EndY=28 EndZ=0
    g13: LineSegment [constr] StartX=-49.5 StartY=-1 StartZ=0 EndX=-49.5 EndY=1 EndZ=0
    g14: GeomPoint [constr] X=-49.5 Y=0 Z=0
    g15: ArcOfCircle CenterX=0 CenterY=0 CenterZ=0 NormalX=0 NormalY=0 NormalZ=1 AngleXU=0 Radius=47 StartAngle=0.638193 EndAngle=2.5034
    g16: LineSegment StartX=37.7492 StartY=28 StartZ=0 EndX=49.5 EndY=28 EndZ=0
    g17: GeomPoint [constr] X=0 Y=-45 Z=0
  constraints (45):
    c: Coincident(g0,g-1)
    c: Coincident(g16,g2)
    c: Coincident(g12,g1)
    c: Horizontal(g1)
    c: Vertical(g2)
    c: Vertical(g3)
    c: Coincident(g4,g5)
    c: Coincident(g5,g6)
    c: Coincident(g8,g7)
    c: Coincident(g7,g4)
    c: Horizontal(g4)
    c: Horizontal(g6)
    c: Vertical(g5)
    c: Vertical(g7)
    c: Diameter(g0) = 65
    c: Symmetric(g1,g2,g0)
    c: DistanceX(g1,g16) = 99
    c: DistanceY(g2,g2) = 56
    c: PointOnObject(g3,g6)
    c: Coincident(g6,g2)
    c: Tangent(g6,g8)
    c: PointOnObject(g8,g3)
    c: Horizontal(g9)
    c: Horizontal(g10)
    c: PointOnObject(g11,g-2)
    c: DistanceY(g4,g11) = 92
    c: DistanceY(g5,g5) = 17
    c: DistanceX(g4,g4) = 129
    c: Coincident(g3,g10)
    c: Coincident(g12,g9)
    c: Tangent(g3,g12)
    c: Coincident(g0,g10)
    c: Coincident(g0,g9)
    c: Coincident(g13,g3)
    c: Coincident(g13,g9)
    c: PointOnObject(g14,g-1)
    c: Symmetric(g9,g3,g14)
    c: DistanceY(g13,g13) = 2
    c: Tangent(g1,g16)
    c: Coincident(g15,g16)
    c: Coincident(g15,g1)
    c: PointOnObject(g11,g15)
    c: Coincident(g15,g0)
    c: PointOnObject(g17,g-2)
    c: Symmetric(g4,g4,g17)
FEATURE [PartDesign::Pad] Pad012
  ClaimChildren = false
  Direction = (1,1,1)
  Fit = 0
  FitJoin = 0
  InnerFit = 0
  InnerFitJoin = 0
  InnerTaperAngle = 0
  InnerTaperAngleRev = 0
  Length = 78
  Length2 = 100
  Linearize = true
  Midplane = true
  NewSolid = false
  Placement = pos=(0,0,0) rot=(1,0,0;1.5708rad)
  Profile = -> Sketch016
  Refine = true
  Suppress = false
  Type = 0
  _ProfileBasedVersion = 0
FEATURE [Sketcher::SketchObject] Sketch017
  ExternalGeometry = -> [Pad012]
  FullyConstrained = true
  MapMode = 5
  Placement = pos=(0,0,28) rot=(0,0,1;3.14159rad)
  Support = -> [Pad012]
  sketch-geometry (5):
    g0: Circle CenterX=43.6246 CenterY=0 CenterZ=0 NormalX=0 NormalY=0 NormalZ=1 AngleXU=0 Radius=4.75
    g1: Circle CenterX=43.6246 CenterY=22.5 CenterZ=0 NormalX=0 NormalY=0 NormalZ=1 AngleXU=0 Radius=4.75
    g2: Circle CenterX=43.6246 CenterY=-22.5 CenterZ=0 NormalX=0 NormalY=0 NormalZ=1 AngleXU=0 Radius=4.75
    g3: GeomPoint [constr] X=37.7492 Y=0 Z=0
    g4: GeomPoint [constr] X=49.5 Y=0 Z=0
  constraints (11):
    c: PointOnObject(g0,g-1)
    c: Equal(g2,g0)
    c: Equal(g0,g1)
    c: Symmetric(g1,g2,g0)
    c: PointOnObject(g3,g-3)
    c: PointOnObject(g4,g-4)
    c: Horizontal(g4,g3)
    c: Symmetric(g4,g3,g0)
    c: Vertical(g1,g0)
    c: Diameter(g1) = 9.5
    c: DistanceY(g2,g1) = 45
FEATURE [PartDesign::Hole] Hole003
  BaseFeature = -> Pad012
  ClaimChildren = false
  CustomThreadClearance = 0
  Depth = 50
  DepthType = 0
  Diameter = 5.8
  DrillForDepth = false
  DrillPoint = 1
  DrillPointAngle = 118
  Fit = 0
  FitJoin = 0
  HoleCutCountersinkAngle = 90
  HoleCutCustomValues = false
  HoleCutDepth = 5.4
  HoleCutDiameter = 9.5
  HoleCutType = 1
  InnerFit = 0
  InnerFitJoin = 0
  ModelThread = false
  NewSolid = false
  Placement = pos=(0,0,0) rot=(1,0,0;1.5708rad)
  Profile = -> Sketch017
  Refine = true
  Suppress = false
  Tapered = false
  TaperedAngle = 90
  ThreadClass = 0
  ThreadDepth = 20
  ThreadDepthType = 1
  ThreadDirection = 0
  ThreadFit = 2
  ThreadSize = 13
  ThreadType = 1
  Threaded = false
  UseCustomThreadClearance = false
  _ProfileBasedVersion = 0
FEATURE [PartDesign::Chamfer] Chamfer002
  Angle = 45
  Base = -> Hole003 [Edge14,Edge25,Edge29,Edge30,Edge31,Edge32,Edge33,Edge35,Edge7,Edge4,Edge27,Edge34,Edge18,Edge17,Edge16,Edge3,Edge6,Edge24,Edge23,Edge22,Edge21,Edge20,Edge19,Edge36,Edge57]
  BaseFeature = -> Hole003
  ChamferType = 0
  FlipDirection = false
  NewSolid = false
  Placement = pos=(0,0,0) rot=(1,0,0;1.5708rad)
  Refine = true
  Size = 1
  Size2 = 1
  SupportTransform = false
  Suppress = false
FEATURE [Sketcher::SketchObject] Sketch018
  FullyConstrained = true
  MapMode = 5
  Placement = pos=(0,0,-28) rot=(0,0,1;3.14159rad)
  Support = -> [Chamfer002]
  sketch-geometry (3):
    g0: Circle CenterX=-57 CenterY=22.5 CenterZ=0 NormalX=0 NormalY=0 NormalZ=1 AngleXU=0 Radius=3.25
    g1: Circle CenterX=-57 CenterY=-22.5 CenterZ=0 NormalX=0 NormalY=0 NormalZ=1 AngleXU=0 Radius=3.25
    g2: GeomPoint [constr] X=-57 Y=0 Z=0
  constraints (7):
    c: PointOnObject(g2,g-1)
    c: Vertical(g0,g1)
    c: Symmetric(g0,g1,g2)
    c: Equal(g0,g1)
    c: Diameter(g0) = 6.5
    c: DistanceX(g0,g-1) = 57
    c: DistanceY(g1,g0) = 45
FEATURE [PartDesign::Pocket] Pocket002
  BaseFeature = -> Chamfer002
  ClaimChildren = false
  Fit = 0
  FitJoin = 0
  InnerFit = 0
  InnerFitJoin = 0
  InnerTaperAngle = 0
  InnerTaperAngleRev = 0
  Length = 5
  Length2 = 100
  Linearize = true
  NewSolid = false
  Placement = pos=(0,0,0) rot=(1,0,0;1.5708rad)
  Profile = -> Sketch018
  Refine = true
  Suppress = false
  Type = 1
  _ProfileBasedVersion = 0
FEATURE [PartDesign::Mirrored] Mirrored001
  BaseFeature = -> Pocket002
  CopyShape = false
  MirrorPlane = -> YZ_Plane004
  NewSolid = false
  OriginalSubs = -> [Pocket002]
  Originals = -> [Pocket002]
  ParallelTransform = true
  Placement = pos=(0,0,0) rot=(1,0,0;1.5708rad)
  Refine = true
  SubTransform = true
  Suppress = false
  _Version = 1
FEATURE [PartDesign::Body] Body004  label="65mm bracket"
  AutoGroupSolids = false
  ExportMode = 0
  Group = -> [Sketch016,Pad012,Sketch017,Hole003,Chamfer002,Sketch018,Pocket002,Mirrored001]
  Origin = -> Origin004
  Placement = pos=(-170,173,-3.84e-14) rot=(1,0,0;4.71239rad)
  Tip = -> Mirrored001
  _ExportChildren = -> [Pad012,Hole003,Chamfer002,Pocket002,Mirrored001]
  _GroupVersion = 1
COMPONENT P5 — recipe-attached ("Link004(0.8KW water)", modeled in this document).
Construction recipe (the document's own serialized feature program — sketch geometry with constraints, then the solid features built on it; lengths are millimeters unless a unit is written):

FEATURE [Sketcher::SketchObject] Sketch013
  FullyConstrained = true
  MapMode = 5
  Support = -> [XY_Plane003]
  sketch-geometry (1):
    g0: Circle CenterX=0 CenterY=0 CenterZ=0 NormalX=0 NormalY=0 NormalZ=1 AngleXU=0 Radius=32.5
  constraints (2):
    c: Coincident(g0,g-1)
    c: Diameter(g0) = 65
FEATURE [PartDesign::Pad] Pad009
  ClaimChildren = false
  Direction = (1,1,1)
  Fit = 0
  FitJoin = 0
  InnerFit = 0
  InnerFitJoin = 0
  InnerTaperAngle = 0
  InnerTaperAngleRev = 0
  Length = 195
  Length2 = 100
  Linearize = true
  NewSolid = false
  Profile = -> Sketch013
  Refine = true
  Suppress = false
  Type = 0
  _ProfileBasedVersion = 0
FEATURE [Sketcher::SketchObject] Sketch014
  FullyConstrained = true
  MapMode = 5
  Placement = pos=(0,0,0) rot=(1,0,0;3.14159rad)
  Support = -> [Pad009]
  sketch-geometry (1):
    g0: Circle CenterX=0 CenterY=0 CenterZ=0 NormalX=0 NormalY=0 NormalZ=1 AngleXU=0 Radius=24
  constraints (2):
    c: Coincident(g0,g-1)
    c: Diameter(g0) = 48
FEATURE [PartDesign::Pad] Pad010
  BaseFeature = -> Pad009
  ClaimChildren = false
  Direction = (1,1,1)
  Fit = 0
  FitJoin = 0
  InnerFit = 0
  InnerFitJoin = 0
  InnerTaperAngle = 0
  InnerTaperAngleRev = 0
  Length = 6.5
  Length2 = 100
  Linearize = true
  NewSolid = false
  Profile = -> Sketch014
  Refine = true
  Suppress = false
  Type = 0
  _ProfileBasedVersion = 0
FEATURE [Sketcher::SketchObject] Sketch015
  FullyConstrained = true
  MapMode = 5
  Placement = pos=(0,0,-6.5) rot=(1,0,0;3.14159rad)
  Support = -> [Pad010]
  sketch-geometry (1):
    g0: Circle CenterX=0 CenterY=0 CenterZ=0 NormalX=0 NormalY=0 NormalZ=1 AngleXU=0 Radius=7
  constraints (2):
    c: Coincident(g0,g-1)
    c: Diameter(g0) = 14
FEATURE [PartDesign::Pad] Pad011
  BaseFeature = -> Pad010
  ClaimChildren = false
  Direction = (1,1,1)
  Fit = 0
  FitJoin = 0
  InnerFit = 0
  InnerFitJoin = 0
  InnerTaperAngle = 0
  InnerTaperAngleRev = 0
  Length = 22.2
  Length2 = 100
  Linearize = true
  NewSolid = false
  Profile = -> Sketch015
  Refine = true
  Suppress = false
  Type = 0
  _ProfileBasedVersion = 0
FEATURE [PartDesign::Hole] Hole002
  BaseFeature = -> Pad011
  ClaimChildren = false
  CustomThreadClearance = 0
  Depth = 40
  DepthType = 0
  Diameter = 3.175
  DrillForDepth = false
  DrillPoint = 1
  DrillPointAngle = 118
  Fit = 0
  FitJoin = 0
  HoleCutCountersinkAngle = 90
  HoleCutCustomValues = false
  HoleCutDepth = 0
  HoleCutDiameter = 6.1
  HoleCutType = 0
  InnerFit = 0
  InnerFitJoin = 0
  ModelThread = false
  NewSolid = false
  Profile = -> Pad011 [Edge9]
  Refine = true
  Suppress = false
  Tapered = false
  TaperedAngle = 90
  ThreadClass = 0
  ThreadDepth = 40
  ThreadDepthType = 0
  ThreadDirection = 0
  ThreadFit = 0
  ThreadSize = 0
  ThreadType = 0
  Threaded = false
  UseCustomThreadClearance = false
  _ProfileBasedVersion = 0
FEATURE [PartDesign::Body] Body003  label="0.8KW water"
  AutoGroupSolids = false
  ExportMode = 0
  Group = -> [Sketch013,Pad009,Sketch014,Pad010,Sketch015,Pad011,Hole002]
  Origin = -> Origin003
  Tip = -> Hole002
  _ExportChildren = -> [Pad009,Pad010,Hole002]
  _GroupVersion = 1
COMPONENT P6 — same part as P2; its construction recipe is shown at P2.
COMPONENT P7 — same part as P3; its construction recipe is shown at P3.
COMPONENT P8 — geometry summary ("Link007(M5x35-Screw)"; no construction recipe available for this part):
  bounding box: 40.0 x 8.5 x 8.5 mm
  tessellated surface: 3,692 triangles
  volume: 923 mm^3 (32% of its bounding box)
  symmetry: revolution-symmetric about the y axis through its bounding-box center; mirror-symmetric across its x mid-plane, z mid-plane
COMPONENT P9 — geometry summary ("Link008(M5x35-Screw)"; no construction recipe available for this part):
  bounding box: 40.0 x 8.5 x 8.5 mm
  tessellated surface: 3,692 triangles
  volume: 923 mm^3 (32% of its bounding box)
  symmetry: revolution-symmetric about the y axis through its bounding-box center; mirror-symmetric across its x mid-plane, z mid-plane
COMPONENT P10 — geometry summary ("1/4inx1in-Screw 4ct"; no construction recipe available for this part):
  bounding box: 123.5 x 54.5 x 31.7 mm
  tessellated surface: 19,760 triangles
  volume: 4673 mm^3 (2% of its bounding box)
  symmetry: 2-fold rotationally symmetric about the y axis; mirror-symmetric across its x mid-plane, z mid-plane
COMPONENT P11 — recipe-attached ("Link010(Makita RT0701C)", modeled in this document).
Construction recipe (the document's own serialized feature program — sketch geometry with constraints, then the solid features built on it; lengths are millimeters unless a unit is written):

FEATURE [Sketcher::SketchObject] Sketch022
  FullyConstrained = true
  MapMode = 5
  Support = -> [XY_Plane006]
  sketch-geometry (1):
    g0: Circle CenterX=0 CenterY=0 CenterZ=0 NormalX=0 NormalY=0 NormalZ=1 AngleXU=0 Radius=32.5
  constraints (2):
    c: Coincident(g0,g-1)
    c: Diameter(g0) = 65
FEATURE [PartDesign::Pad] Pad014
  ClaimChildren = false
  Direction = (1,1,1)
  Fit = 0
  FitJoin = 0
  InnerFit = 0
  InnerFitJoin = 0
  InnerTaperAngle = 0
  InnerTaperAngleRev = 0
  Length = 85.5
  Length2 = 100
  Linearize = true
  NewSolid = false
  Profile = -> Sketch022
  Refine = true
  Suppress = false
  Type = 0
  _ProfileBasedVersion = 1
FEATURE [Sketcher::SketchObject] Sketch023
  FullyConstrained = true
  MapMode = 5
  Placement = pos=(0,0,0) rot=(1,0,0;3.14159rad)
  Support = -> [Pad014]
  sketch-geometry (1):
    g0: Circle CenterX=0 CenterY=0 CenterZ=0 NormalX=0 NormalY=0 NormalZ=1 AngleXU=0 Radius=21.5
  constraints (2):
    c: Coincident(g0,g-1)
    c: Diameter(g0) = 43
FEATURE [PartDesign::Pad] Pad015
  BaseFeature = -> Pad014
  ClaimChildren = false
  Direction = (1,1,1)
  Fit = 0
  FitJoin = 0
  InnerFit = 0
  InnerFitJoin = 0
  InnerTaperAngle = 0
  InnerTaperAngleRev = 0
  Length = 8
  Length2 = 100
  Linearize = true
  NewSolid = false
  Profile = -> Sketch023
  Refine = true
  Suppress = false
  Type = 0
  _ProfileBasedVersion = 1
FEATURE [Sketcher::SketchObject] Sketch024
  FullyConstrained = true
  MapMode = 5
  Placement = pos=(0,0,-8) rot=(1,0,0;3.14159rad)
  Support = -> [Pad015]
  sketch-geometry (2):
    g0: Circle CenterX=0 CenterY=0 CenterZ=0 NormalX=0 NormalY=0 NormalZ=1 AngleXU=0 Radius=8.3
    g1: Circle CenterX=0 CenterY=0 CenterZ=0 NormalX=0 NormalY=0 NormalZ=1 AngleXU=0 Radius=3.175
  constraints (4):
    c: Coincident(g0,g-1)
    c: Diameter(g0) = 16.6
    c: Coincident(g1,g0)
    c: Diameter(g1) = 6.35
FEATURE [PartDesign::Pad] Pad016
  BaseFeature = -> Pad015
  ClaimChildren = false
  Direction = (1,1,1)
  Fit = 0
  FitJoin = 0
  InnerFit = 0
  InnerFitJoin = 0
  InnerTaperAngle = 0
  InnerTaperAngleRev = 0
  Length = 24.5
  Length2 = 100
  Linearize = true
  NewSolid = false
  Profile = -> Sketch024
  Refine = true
  Suppress = false
  Type = 0
  _ProfileBasedVersion = 1
FEATURE [Sketcher::SketchObject] Sketch025
  ExternalGeometry = -> [Pad016]
  FullyConstrained = false
  MapMode = 5
  Placement = pos=(0,0,0) rot=(1,0,0;3.14159rad)
  Support = -> [Pad016]
  sketch-geometry (6):
    g0: ArcOfCircle CenterX=0 CenterY=0 CenterZ=0 NormalX=0 NormalY=0 NormalZ=1 AngleXU=0 Radius=21.5 StartAngle=3.40339 EndAngle=4.45059
    g1: LineSegment StartX=-15.8177 StartY=-0.614862 StartZ=0 EndX=-0.614862 EndY=-15.8177 EndZ=0
    g2: LineSegment StartX=-0.614862 StartY=-15.8177 StartZ=0 EndX=-5.56461 EndY=-20.7674 EndZ=0
    g3: LineSegment StartX=-15.8177 StartY=-0.614862 StartZ=0 EndX=-20.7674 EndY=-5.56461 EndZ=0
    g4: LineSegment [constr] StartX=0 StartY=0 StartZ=0 EndX=-24.9637 EndY=-24.9637 EndZ=0
    g5: GeomPoint [constr] X=-8.21626 Y=-8.21626 Z=0
  constraints (16):
    c: Coincident(g0,g-3)
    c: Equal(g0,g-3)
    c: Coincident(g1,g2)
    c: Coincident(g1,g3)
    c: Parallel(g3,g2)
    c: Equal(g3,g2)
    c: Perpendicular(g1,g3)
    c: Coincident(g4,g0)
    c: Angle(g4,g-1) = 2.35619
    c: Parallel(g3,g4)
    c: Distance(g1) = 21.5
    c: Distance(g3) = 7
    c: PointOnObject(g5,g1)
    c: PointOnObject(g5,g4)
    c: Coincident(g0,g3)
    c: Coincident(g0,g2)
FEATURE [PartDesign::Pad] Pad017
  BaseFeature = -> Pad016
  ClaimChildren = false
  Direction = (1,1,1)
  Fit = 0
  FitJoin = 0
  InnerFit = 0
  InnerFitJoin = 0
  InnerTaperAngle = 0
  InnerTaperAngleRev = 0
  Length = 17
  Length2 = 100
  Linearize = true
  NewSolid = false
  Profile = -> Sketch025
  Refine = true
  Suppress = false
  Type = 0
  _ProfileBasedVersion = 1
FEATURE [PartDesign::Chamfer] Chamfer004
  Angle = 45
  Base = -> Pad017 [Edge1]
  BaseFeature = -> Pad017
  ChamferType = 0
  FlipDirection = false
  NewSolid = false
  Refine = true
  Size = 2
  Size2 = 1
  SupportTransform = false
  Suppress = false
FEATURE [PartDesign::Chamfer] Chamfer005
  Angle = 45
  Base = -> Chamfer004 [Edge19,Edge10]
  BaseFeature = -> Chamfer004
  ChamferType = 0
  FlipDirection = false
  NewSolid = false
  Refine = true
  Size = 5
  Size2 = 1
  SupportTransform = false
  Suppress = false
FEATURE [PartDesign::Chamfer] Chamfer006
  Angle = 45
  Base = -> Chamfer005 [Edge34]
  BaseFeature = -> Chamfer005
  ChamferType = 0
  FlipDirection = false
  NewSolid = false
  Refine = true
  Size = 1
  Size2 = 1
  SupportTransform = false
  Suppress = false
FEATURE [PartDesign::Plane] DatumPlane
  AttachmentOffset = pos=(0,0,-1) rot=(0,0,1;0rad)
  Length = 256.946
  MapMode = 5
  MinimumLength = 10
  MinimumWidth = 10
  Placement = pos=(-8.92337,8.92337,0) rot=(0.862856,0.357407,0.357407;1.71777rad)
  ResizeMode = 0
  Support = -> [Chamfer006]
  Width = 281.338
FEATURE [Sketcher::SketchObject] Sketch026
  FullyConstrained = true
  MapMode = 5
  Placement = pos=(-8.92337,8.92337,0) rot=(-0.281085,0.678598,0.678598;3.68962rad)
  Support = -> [DatumPlane]
  sketch-geometry (4):
    g0: ArcOfCircle CenterX=0 CenterY=-12.35 CenterZ=0 NormalX=0 NormalY=0 NormalZ=1 AngleXU=0 Radius=6.65 StartAngle=3.14159 EndAngle=6.28319
    g1: LineSegment StartX=-6.65 StartY=-12.35 StartZ=0 EndX=-6.65 EndY=0 EndZ=0
    g2: LineSegment StartX=-6.65 StartY=0 StartZ=0 EndX=6.65 EndY=0 EndZ=0
    g3: LineSegment StartX=6.65 StartY=0 StartZ=0 EndX=6.65 EndY=-12.35 EndZ=0
  constraints (11):
    c: PointOnObject(g0,g-2)
    c: Vertical(g1)
    c: Coincident(g2,g1)
    c: Horizontal(g2)
    c: Coincident(g3,g2)
    c: Vertical(g3)
    c: Tangent(g0,g3) = 1.5708
    c: Tangent(g0,g1) = 1.5708
    c: Diameter(g0) = 13.3
    c: DistanceY(g0,g-1) = 12.35
    c: Horizontal(g2,g-1)
FEATURE [PartDesign::Pad] Pad018
  BaseFeature = -> Chamfer006
  ClaimChildren = false
  Direction = (1,1,1)
  Fit = 0
  FitJoin = 0
  InnerFit = 0
  InnerFitJoin = 0
  InnerTaperAngle = 0
  InnerTaperAngleRev = 0
  Length = 10.5
  Length2 = 100
  Linearize = true
  NewSolid = false
  Profile = -> Sketch026
  Refine = true
  Suppress = false
  Type = 0
  _ProfileBasedVersion = 1
FEATURE [Sketcher::SketchObject] Sketch027
  ExternalGeometry = -> [Pad018]
  FullyConstrained = true
  MapMode = 5
  Placement = pos=(-16.348,16.348,4.4e-15) rot=(-0.281085,0.678598,0.678598;3.68962rad)
  Support = -> [Pad018]
  sketch-geometry (1):
    g0: Circle CenterX=1e-14 CenterY=-12.35 CenterZ=0 NormalX=0 NormalY=0 NormalZ=1 AngleXU=0 Radius=5.35
  constraints (2):
    c: Coincident(g0,g-3)
    c: Diameter(g0) = 10.7
FEATURE [PartDesign::Pad] Pad019
  BaseFeature = -> Pad018
  ClaimChildren = false
  Direction = (1,1,1)
  Fit = 0
  FitJoin = 0
  InnerFit = 0
  InnerFitJoin = 0
  InnerTaperAngle = 0
  InnerTaperAngleRev = 0
  Length = 3.5
  Length2 = 100
  Linearize = true
  NewSolid = false
  Profile = -> Sketch027
  Refine = true
  Suppress = false
  Type = 0
  _ProfileBasedVersion = 1
FEATURE [PartDesign::Fillet] Fillet
  Base = -> Pad019 [Edge55,Edge47,Edge19,Edge20,Edge18,Edge35,Edge9,Edge7,Edge3,Edge1,Edge2,Edge4,Edge11]
  BaseFeature = -> Pad019
  NewSolid = false
  Radius = 0.5
  Refine = true
  SupportTransform = false
  Suppress = false
FEATURE [Sketcher::SketchObject] Sketch028
  ExternalGeometry = -> [Fillet]
  FullyConstrained = true
  MapMode = 5
  Placement = pos=(0,0,0) rot=(1,0,0;3.14159rad)
  Support = -> [Fillet]
  sketch-geometry (4):
    g0: LineSegment StartX=2.35 StartY=-32.4149 StartZ=0 EndX=2.35 EndY=-30.9149 EndZ=0
    g1: LineSegment StartX=2.35 StartY=-30.9149 StartZ=0 EndX=-2.35 EndY=-30.9149 EndZ=0
    g2: LineSegment StartX=-2.35 StartY=-30.9149 StartZ=0 EndX=-2.35 EndY=-32.4149 EndZ=0
    g3: ArcOfCircle CenterX=0 CenterY=0 CenterZ=0 NormalX=0 NormalY=0 NormalZ=1 AngleXU=0 Radius=32.5 StartAngle=4.64002 EndAngle=4.78476
  constraints (11):
    c: Coincident(g0,g1)
    c: Coincident(g1,g2)
    c: Vertical(g0)
    c: Vertical(g2)
    c: Coincident(g3,g-3)
    c: Equal(g3,g-3)
    c: Coincident(g0,g3)
    c: Coincident(g3,g2)
    c: DistanceX(g1,g1) = 4.7
    c: Symmetric(g0,g1,g-2)
    c: DistanceY(g0,g0) = 1.5
FEATURE [PartDesign::Pocket] Pocket004
  BaseFeature = -> Fillet
  ClaimChildren = false
  Fit = 0
  FitJoin = 0
  InnerFit = 0
  InnerFitJoin = 0
  InnerTaperAngle = 0
  InnerTaperAngleRev = 0
  Length = 57
  Length2 = 100
  Linearize = true
  NewSolid = false
  Profile = -> Sketch028
  Refine = true
  Suppress = false
  Type = 0
  _ProfileBasedVersion = 1
FEATURE [Sketcher::SketchObject] Sketch029
  FullyConstrained = true
  MapMode = 5
  Placement = pos=(0,0,85.5) rot=(0,0,1;0rad)
  Support = -> [Pocket004]
  sketch-geometry (1):
    g0: Circle CenterX=0 CenterY=0 CenterZ=0 NormalX=0 NormalY=0 NormalZ=1 AngleXU=0 Radius=33
  constraints (2):
    c: Coincident(g0,g-1)
    c: Diameter(g0) = 66
FEATURE [PartDesign::Pad] Pad020
  BaseFeature = -> Pocket004
  ClaimChildren = false
  Direction = (1,1,1)
  Fit = 0
  FitJoin = 0
  InnerFit = 0
  InnerFitJoin = 0
  InnerTaperAngle = 0
  InnerTaperAngleRev = 0
  Length = 7.5
  Length2 = 100
  Linearize = true
  NewSolid = false
  Profile = -> Sketch029
  Refine = true
  Suppress = false
  Type = 0
  _ProfileBasedVersion = 1
FEATURE [PartDesign::Plane] DatumPlane001
  AttachmentOffset = pos=(0,0,3.5) rot=(0,0,1;0rad)
  Length = 231.5
  MapMode = 5
  MinimumLength = 10
  MinimumWidth = 10
  Placement = pos=(0,0,-36) rot=(1,0,0;3.14159rad)
  ResizeMode = 0
  Support = -> [Pad020]
  Width = 131.877
FEATURE [Sketcher::SketchObject] Sketch030
  FullyConstrained = true
  MapMode = 5
  Placement = pos=(0,0,-36) rot=(1,0,0;3.14159rad)
  Support = -> [DatumPlane001]
  sketch-geometry (8):
    g0: Circle CenterX=0 CenterY=0 CenterZ=0 NormalX=0 NormalY=0 NormalZ=1 AngleXU=0 Radius=5
    g1: LineSegment StartX=8.83883 StartY=-8.83883 StartZ=0 EndX=12.0741 EndY=3.23524 EndZ=0
    g2: LineSegment StartX=12.0741 StartY=3.23524 StartZ=0 EndX=3.23524 EndY=12.0741 EndZ=0
    g3: LineSegment StartX=3.23524 StartY=12.0741 StartZ=0 EndX=-8.83883 EndY=8.83883 EndZ=0
    g4: LineSegment StartX=-8.83883 StartY=8.83883 StartZ=0 EndX=-12.0741 EndY=-3.23524 EndZ=0
    g5: LineSegment StartX=-12.0741 StartY=-3.23524 StartZ=0 EndX=-3.23524 EndY=-12.0741 EndZ=0
    g6: LineSegment StartX=-3.23524 StartY=-12.0741 StartZ=0 EndX=8.83883 EndY=-8.83883 EndZ=0
    g7: Circle [constr] CenterX=0 CenterY=0 CenterZ=0 NormalX=0 NormalY=0 NormalZ=1 AngleXU=0 Radius=12.5
  constraints (18):
    c: Coincident(g0,g-1)
    c: Diameter(g0) = 10
    c: Coincident(g1,g2)
    c: Coincident(g2,g3)
    c: Coincident(g3,g4)
    c: Coincident(g4,g5)
    c: Coincident(g5,g6)
    c: Coincident(g6,g1)
    c: Equal(g1, g2-g6) x5
    c: PointOnObject(g1,g7)
    c: PointOnObject(g2,g7)
    c: PointOnObject(g3,g7)
    c: PointOnObject(g4,g7)
    c: PointOnObject(g5,g7)
    c: PointOnObject(g6,g7)
    c: Coincident(g7,g0)
    c: Angle(g5,g-1) = 0.785398
    c: Diameter(g7) = 25
FEATURE [PartDesign::Pad] Pad021
  BaseFeature = -> Pad020
  ClaimChildren = false
  Direction = (1,1,1)
  Fit = 0
  FitJoin = 0
  InnerFit = 0
  InnerFitJoin = 0
  InnerTaperAngle = 0
  InnerTaperAngleRev = 0
  Length = 12
  Length2 = 100
  Linearize = true
  NewSolid = false
  Profile = -> Sketch030
  Refine = true
  Reversed = true
  Suppress = false
  Type = 0
  _ProfileBasedVersion = 1
FEATURE [Sketcher::SketchObject] Sketch031
  ExternalGeometry = -> [Pad021]
  FullyConstrained = true
  MapMode = 5
  Placement = pos=(0,0,0) rot=(0.57735,0.57735,0.57735;2.0944rad)
  Support = -> [YZ_Plane006]
  sketch-geometry (6):
    g0: LineSegment StartX=-15 StartY=-28.5 StartZ=0 EndX=-9 EndY=-22.5 EndZ=0
    g1: LineSegment StartX=-9 StartY=-22.5 StartZ=0 EndX=-19 EndY=-22.5 EndZ=0
    g2: LineSegment StartX=-19 StartY=-22.5 StartZ=0 EndX=-19 EndY=-37.5 EndZ=0
    g3: LineSegment StartX=-19 StartY=-37.5 StartZ=0 EndX=-9 EndY=-37.5 EndZ=0
    g4: LineSegment StartX=-9 StartY=-37.5 StartZ=0 EndX=-15 EndY=-31.5 EndZ=0
    g5: LineSegment StartX=-15 StartY=-31.5 StartZ=0 EndX=-15 EndY=-28.5 EndZ=0
  constraints (18):
    c: Horizontal(g1)
    c: Coincident(g1,g2)
    c: Coincident(g2,g3)
    c: Horizontal(g3)
    c: Coincident(g3,g4)
    c: Coincident(g4,g5)
    c: Coincident(g5,g0)
    c: Vertical(g5)
    c: Coincident(g0,g1)
    c: Angle(g1,g0) = 0.785398
    c: Angle(g4,g3) = 0.785398
    c: DistanceY(g3,g-3) = 1.5
    c: DistanceY(g-3,g0) = 1.5
    c: DistanceX(g1,g1) = 10
    c: Vertical(g2)
    c: Vertical(g3,g0)
    c: DistanceX(g3,g-1) = 9
    c: DistanceY(g5,g5) = 3
FEATURE [PartDesign::Groove] Groove002
  Angle = 360
  Axis = (-3e-16,3e-16,1)
  Base = (0,0,0)
  BaseFeature = -> Pad021
  ClaimChildren = false
  Fit = 0
  FitJoin = 0
  InnerFit = 0
  InnerFitJoin = 0
  NewSolid = false
  Profile = -> Sketch031
  ReferenceAxis = -> Z_Axis006
  Refine = true
  Reversed = true
  Suppress = false
  _ProfileBasedVersion = 1
FEATURE [PartDesign::Body] Body006  label="Makita RT0701C"
  AutoGroupSolids = false
  ExportMode = 0
  Group = -> [Sketch022,Pad014,Sketch023,Pad015,Sketch024,Pad016,Sketch025,Pad017,Chamfer004,Chamfer005,Chamfer006,DatumPlane,Sketch026,Pad018,Sketch027,Pad019,Fillet,Sketch028,Pocket004,Sketch029,Pad020,DatumPlane001,Sketch030,Pad021,Sketch031,Groove002]
  Origin = -> Origin006
  Tip = -> Groove002
  _ExportChildren = -> [Pad014,Pad015,Pad016,Pad017,Chamfer004,Chamfer005,Chamfer006,DatumPlane,Pad018,Pad019,Fillet,Pocket004,Pad020,DatumPlane001,Pad021,Groove002]
  _GroupVersion = 1
COMPONENT P12 — same part as P4; its construction recipe is shown at P4.
COMPONENT P13 — same part as P3; its construction recipe is shown at P3.
COMPONENT P14 — geometry summary ("Link013(1/4inx1in-Screw)"; no construction recipe available for this part):
  bounding box: 123.5 x 54.5 x 31.7 mm
  tessellated surface: 19,760 triangles
  volume: 4673 mm^3 (2% of its bounding box)
  symmetry: 2-fold rotationally symmetric about the y axis; mirror-symmetric across its x mid-plane, z mid-plane
PROVENANCE & LICENSES
A FreeCAD (.FCStd) document from a public repository crawl; recipes are the document's own serialized feature recipes (and, for linked parts, companion documents' recipes).
License: mit.
